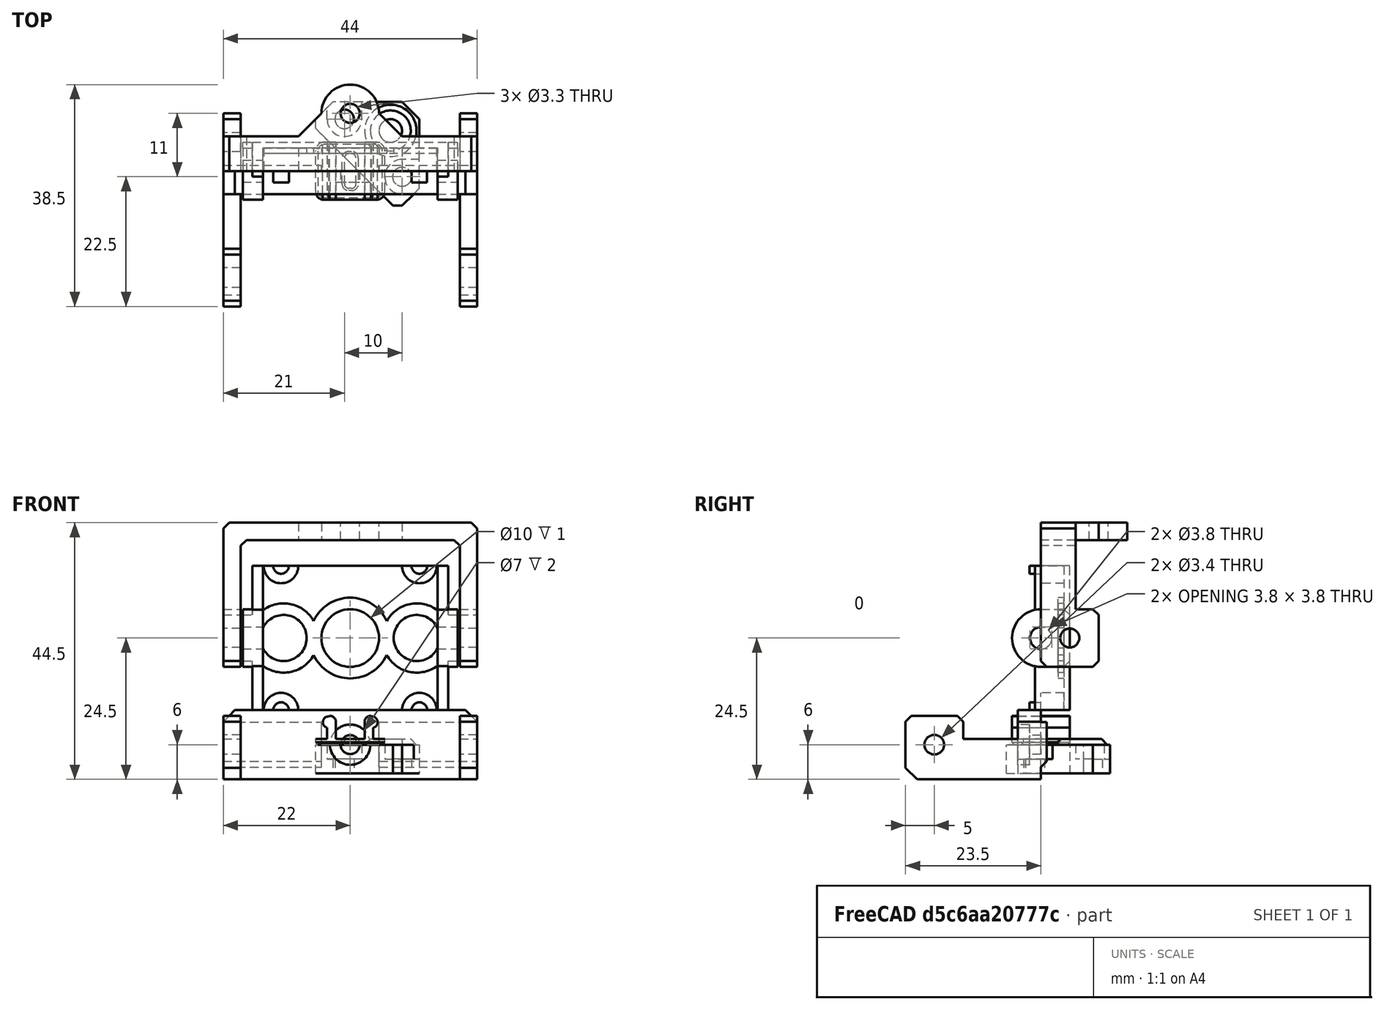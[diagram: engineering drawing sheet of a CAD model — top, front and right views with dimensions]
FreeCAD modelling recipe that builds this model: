
FCSTD DOCUMENT  (FreeCAD 0.19R24291 (Git))
Label: camera-mount
License: Other
LicenseURL: GPL3
objects: Part::Box×11, Part::Chamfer×7, Part::Cylinder×5, Part::Feature×3, Part::MultiFuse×3, Part::Cut×3, Part::Fillet×3, Part::Refine×1
note: 36 computed .brp shape members not serialized (recipe doc carries the construction recipe); baked Part::Feature solids carry a one-line shape summary decoded from their .brp

FEATURE [Part::Feature] Cut002008023012009006003002007002  label="corner-mount"
  Placement = pos=(0,0,0) rot=(0,1,0;3.14159rad)
  shape: bbox 18 x 18 x 6 mm, 23 faces (baked)
FEATURE [Part::Feature] Cut002008023012009006003002007003001001  label="camera-back-plate003"
  Placement = pos=(0,-5,39) rot=(0,0,1;0rad)
  shape: bbox 37.3 x 10 x 25 mm, 58 faces (baked)
FEATURE [Part::Feature] Chamfer004001002001001  label="camera-arm003"
  Placement = pos=(0,0,39) rot=(0,0,1;0rad)
  shape: bbox 44 x 15 x 25 mm, 33 faces (baked)
FEATURE [Part::Cylinder] Cylinder
  Angle = 360
  AttacherType = Attacher::AttachEngine3D
  Height = 10
  Placement = pos=(0,0,-2) rot=(0,0,1;0rad)
  Radius = 1.65
FEATURE [Part::Box] Box  label="Cube"
  AttacherType = Attacher::AttachEngine3D
  Height = 4
  Length = 44
  Placement = pos=(-22,-6,0) rot=(0,0,1;0rad)
  Width = 12
FEATURE [Part::Box] Box001  label="Cube001"
  AttacherType = Attacher::AttachEngine3D
  Height = 23.5
  Length = 3
  Placement = pos=(-22,-6,0) rot=(0,0,1;0rad)
  Width = 7
FEATURE [Part::Box] Box002  label="Cube002"
  AttacherType = Attacher::AttachEngine3D
  Height = 23.5
  Length = 3
  Placement = pos=(19,-6,0) rot=(0,0,1;0rad)
  Width = 7
FEATURE [Part::Box] Box003  label="Cube003"
  AttacherType = Attacher::AttachEngine3D
  Height = 10
  Length = 3
  Placement = pos=(19,-6,13.5) rot=(0,0,1;0rad)
  Width = 11
FEATURE [Part::Box] Box004  label="Cube004"
  AttacherType = Attacher::AttachEngine3D
  Height = 10
  Length = 3
  Placement = pos=(-22,-6,13.5) rot=(0,0,1;0rad)
  Width = 11
FEATURE [Part::Cylinder] Cylinder001
  Angle = 360
  AttacherType = Attacher::AttachEngine3D
  Height = 5
  Placement = pos=(0,0,2) rot=(0,0,1;0rad)
  Radius = 3.5
FEATURE [Part::MultiFuse] Fusion
  Shapes = -> [Cylinder,Cylinder001]
FEATURE [Part::Box] Box005  label="Cube005"
  AttacherType = Attacher::AttachEngine3D
  Height = 1
  Length = 17
  Placement = pos=(-22,-3.9,-1) rot=(0,0,1;0rad)
  Width = 7.8
FEATURE [Part::Box] Box006  label="Cube006"
  AttacherType = Attacher::AttachEngine3D
  Height = 1
  Length = 17
  Placement = pos=(5,-3.9,-1) rot=(0,0,1;0rad)
  Width = 7.8
FEATURE [Part::MultiFuse] Fusion001
  Shapes = -> [Box006,Box005,Box004,Box003,Box002,Box001,Box]
FEATURE [Part::Chamfer] Chamfer
  Base = -> Fusion001
  Edges = 2 edges r=0.99: [Edge5,Edge29]
FEATURE [Part::Cut] Cut
  Base = -> Chamfer
  Tool = -> Fusion
FEATURE [Part::Chamfer] Chamfer004001002001002
  Base = -> Cut
  Edges = 4 edges r=1: [Edge98,Edge103,Edge114,Edge118]
FEATURE [Part::Chamfer] Chamfer004001002001003
  Base = -> Chamfer004001002001002
  Edges = 2 edges r=2: [Edge39,Edge127]
FEATURE [Part::Chamfer] Chamfer004001002001004
  Base = -> Chamfer004001002001003
  Edges = 2 edges r=2: [Edge51,Edge67]
FEATURE [Part::Cylinder] Cylinder002
  Angle = 360
  AttacherType = Attacher::AttachEngine3D
  Height = 48
  Placement = pos=(24,0,18.5) rot=(0,1,0;4.71239rad)
  Radius = 1.7
FEATURE [Part::Cut] Cut002008023012009006003002007003001002  label="back-mount"
  Base = -> Chamfer004001002001004
  Placement = pos=(0,0,0) rot=(1,0,0;1.5708rad)
  Tool = -> Cylinder002
FEATURE [Part::Refine] Cut002008023012009006003002007003001002001  label="back-mount001"
  Source = -> Cut002008023012009006003002007003001002
FEATURE [Part::Box] Box007  label="Cube007"
  AttacherType = Attacher::AttachEngine3D
  Height = 1
  Length = 12
  Placement = pos=(-6,-5,0) rot=(0,0,1;0rad)
  Width = 10
FEATURE [Part::Box] Box008  label="Cube008"
  AttacherType = Attacher::AttachEngine3D
  Height = 5
  Length = 1.5
  Placement = pos=(-4,-5,0) rot=(0,0,1;0rad)
  Width = 10
FEATURE [Part::Box] Box009  label="Cube009"
  AttacherType = Attacher::AttachEngine3D
  Height = 5
  Length = 1.5
  Placement = pos=(2.5,-5,0) rot=(0,0,1;0rad)
  Width = 10
FEATURE [Part::Cylinder] Cylinder003
  Angle = 360
  AttacherType = Attacher::AttachEngine3D
  Height = 10
  Placement = pos=(-3.75,-5,3.9) rot=(1,0,0;4.71239rad)
  Radius = 1
FEATURE [Part::Cylinder] Cylinder004
  Angle = 360
  AttacherType = Attacher::AttachEngine3D
  Height = 10
  Placement = pos=(3.75,-5,3.9) rot=(-1,0,0;1.5708rad)
  Radius = 1
FEATURE [Part::Chamfer] Chamfer004001002001005
  Base = -> Box008
  Edges = 1 edges r=0.4: [Edge2]
FEATURE [Part::Chamfer] Chamfer004001002001006
  Base = -> Box009
  Edges = 1 edges r=0.4: [Edge6]
FEATURE [Part::MultiFuse] Fusion002
  Shapes = -> [Chamfer004001002001006,Chamfer004001002001005,Cylinder004,Cylinder003,Box007]
FEATURE [Part::Box] Box010  label="Cube010"
  AttacherType = Attacher::AttachEngine3D
  Height = 10
  Length = 2
  Placement = pos=(-1,-3,0) rot=(0,0,1;0rad)
  Width = 6
FEATURE [Part::Cut] Cut002008023012009006003002007003001002002
  Base = -> Fusion002
  Tool = -> Box010
FEATURE [Part::Fillet] Fillet
  Base = -> Cut002008023012009006003002007003001002002
  Edges = 4 edges r=0.75: [Edge58,Edge59,Edge61,Edge63]
FEATURE [Part::Fillet] Fillet001
  Base = -> Fillet
  Edges = 4 edges r=1.5: [Edge78,Edge82,Edge98,Edge102]
FEATURE [Part::Chamfer] Chamfer004001002001007
  Base = -> Fillet001
  Edges = 23 edges r=0.4: [Edge6,Edge7,Edge8,Edge9,Edge14,Edge20,Edge29,Edge34,Edge35,Edge36,Edge37,Edge38,Edge39,Edge40,Edge41,Edge43,Edge67,Edge81,Edge93,Edge98,Edge99,Edge100,Edge101]
FEATURE [Part::Fillet] Fillet002  label="cable-clip"
  Base = -> Chamfer004001002001007
  Edges = 2 edges r=1: [Edge51,Edge110]
